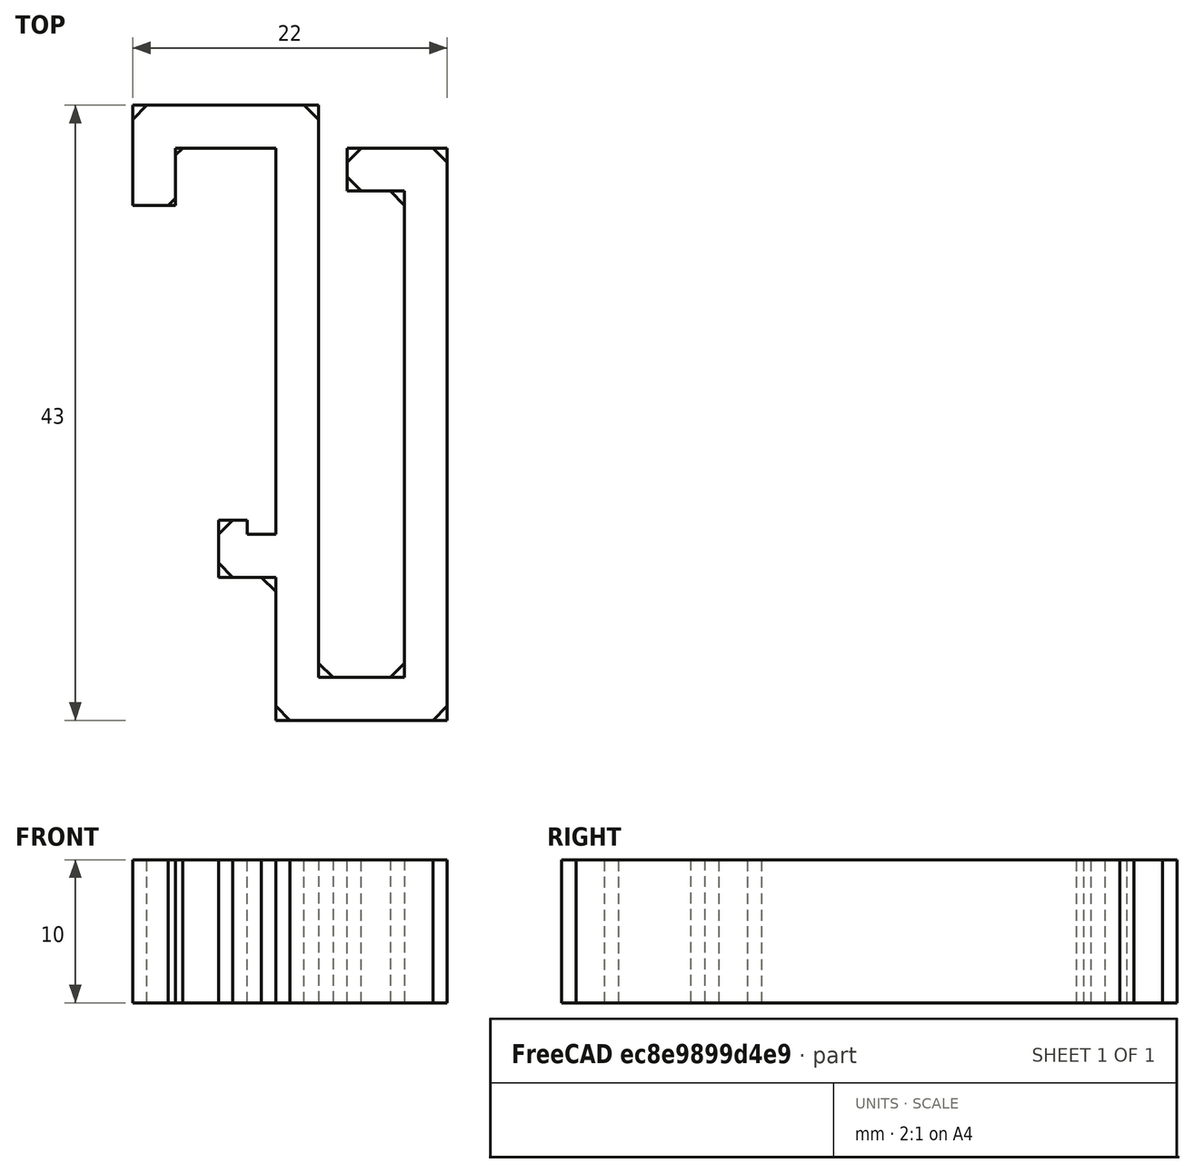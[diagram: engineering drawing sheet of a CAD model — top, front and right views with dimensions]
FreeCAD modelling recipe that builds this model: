
FCSTD DOCUMENT  (FreeCAD 0.18R14555 (Git shallow))
Label: 4040-extrusion-clip
License: All rights reserved
LicenseURL: http://en.wikipedia.org/wiki/All_rights_reserved
objects: Part::Chamfer×12, Part::Box×8, Part::Feature×2, Part::MultiFuse×1
note: 23 computed .brp shape members not serialized (recipe doc carries the construction recipe); baked Part::Feature solids carry a one-line shape summary decoded from their .brp

FEATURE [Part::Box] Box  label="Cube"
  AttacherType = Attacher::AttachEngine3D
  Height = 10
  Length = 3
  Width = 43
FEATURE [Part::Box] Box001  label="Cube001"
  AttacherType = Attacher::AttachEngine3D
  Height = 10
  Length = 12
  Width = 3
FEATURE [Part::Box] Box002  label="Cube002"
  AttacherType = Attacher::AttachEngine3D
  Height = 10
  Length = 3
  Placement = pos=(9,0,0) rot=(0,0,1;0rad)
  Width = 40
FEATURE [Part::Box] Box003  label="Cube003"
  AttacherType = Attacher::AttachEngine3D
  Height = 10
  Length = 13
  Placement = pos=(-10,40,0) rot=(0,0,1;0rad)
  Width = 3
FEATURE [Part::Box] Box004  label="Cube004"
  AttacherType = Attacher::AttachEngine3D
  Height = 10
  Length = 3
  Placement = pos=(-10,36,0) rot=(0,0,1;0rad)
  Width = 7
FEATURE [Part::Box] Box006  label="Cube006"
  AttacherType = Attacher::AttachEngine3D
  Height = 10
  Length = 7
  Placement = pos=(5,37,0) rot=(0,0,1;0rad)
  Width = 3
FEATURE [Part::Box] Box007  label="Cube007"
  AttacherType = Attacher::AttachEngine3D
  Height = 10
  Length = 7
  Placement = pos=(-4,10,0) rot=(0,0,1;0rad)
  Width = 3
FEATURE [Part::Box] Box008  label="Cube008"
  AttacherType = Attacher::AttachEngine3D
  Height = 10
  Length = 2
  Placement = pos=(-4,10,0) rot=(0,0,1;0rad)
  Width = 4
FEATURE [Part::MultiFuse] Fusion
  Shapes = -> [Box006,Box008,Box004,Box007,Box003,Box002,Box001,Box]
FEATURE [Part::Feature] Fusion001
  shape: bbox 22 x 43 x 10 mm, 22 faces (baked)
FEATURE [Part::Chamfer] Chamfer
  Base = -> Fusion001
  Edges = 1 edges r=0.5: [Edge38]
FEATURE [Part::Chamfer] Chamfer001
  Base = -> Chamfer
  Edges = 1 edges r=0.5: [Edge23]
FEATURE [Part::Chamfer] Chamfer002
  Base = -> Chamfer001
  Edges = 1 edges r=1: [Edge49]
FEATURE [Part::Chamfer] Chamfer003
  Base = -> Chamfer002
  Edges = 2 edges r=1: [Edge61,Edge66]
FEATURE [Part::Chamfer] Chamfer004
  Base = -> Chamfer003
  Edges = 2 edges r=1: [Edge65,Edge70]
FEATURE [Part::Chamfer] Chamfer005
  Base = -> Chamfer004
  Edges = 2 edges r=1: [Edge46,Edge50]
FEATURE [Part::Chamfer] Chamfer006
  Base = -> Chamfer005
  Edges = 1 edges r=1: [Edge31]
FEATURE [Part::Chamfer] Chamfer007
  Base = -> Chamfer006
  Edges = 1 edges r=1: [Edge42]
FEATURE [Part::Chamfer] Chamfer008
  Base = -> Chamfer007
  Edges = 1 edges r=1: [Edge33]
FEATURE [Part::Chamfer] Chamfer009
  Base = -> Chamfer008
  Edges = 1 edges r=1: [Edge67]
FEATURE [Part::Chamfer] Chamfer010
  Base = -> Chamfer009
  Edges = 1 edges r=1: [Edge55]
FEATURE [Part::Chamfer] Chamfer011
  Base = -> Chamfer010
  Edges = 1 edges r=1: [Edge52]
FEATURE [Part::Feature] Chamfer011_solid  label="Chamfer011 (Solid)"
  shape: bbox 22 x 43 x 10 mm, 37 faces (baked)
